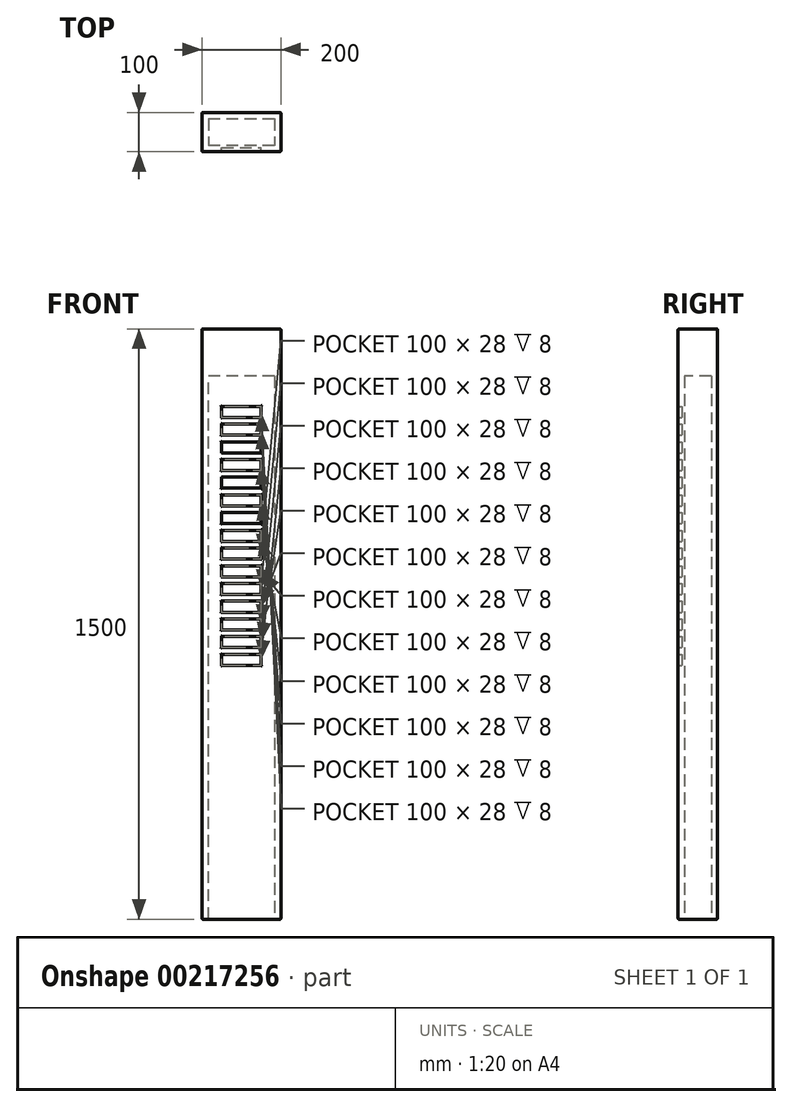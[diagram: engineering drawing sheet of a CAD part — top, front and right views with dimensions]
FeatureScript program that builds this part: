
annotation { "Feature Type Name" : "Feature", "Feature Type Description" : "" }
export const myFeature = defineFeature(function(context is Context, id is Id, definition is map)
    precondition{}
    {
        {
            var Q0;
            Q0=qCreatedBy(makeId("Front.planeOp"),FACE);
            var sketch = newSketch(context, id + "F0", { "sketchPlane" : qUnion([Q0])});
            skLineSegment(sketch, "E0.bottom", {"start": v(-100, 747.5) * mm, "end": v(100, 747.5) * mm});
            skLineSegment(sketch, "E0.top", {"start": v(-100, -752.5) * mm, "end": v(100, -752.5) * mm});
            skLineSegment(sketch, "E0.left", {"start": v(-100, 747.5) * mm, "end": v(-100, -752.5) * mm});
            skLineSegment(sketch, "E0.right", {"start": v(100, 747.5) * mm, "end": v(100, -752.5) * mm});
            skLineSegment(sketch, "E1.top", {"start": v(-50, 522.5) * mm, "end": v(50, 522.5) * mm});
            skPoint(sketch, "E1.middle", {"position": v(0, 535) * mm});
            skLineSegment(sketch, "E2.top", {"start": v(-50, 477.5) * mm, "end": v(50, 477.5) * mm});
            skPoint(sketch, "E2.middle", {"position": v(0, 490) * mm});
            skLineSegment(sketch, "E3.top", {"start": v(-50, 432.5) * mm, "end": v(50, 432.5) * mm});
            skPoint(sketch, "E3.middle", {"position": v(0, 445) * mm});
            skPoint(sketch, "E4.middle", {"position": v(0, 400) * mm});
            skLineSegment(sketch, "E5.bottom", {"start": v(-50, 387.1) * mm, "end": v(50, 387.1) * mm});
            skLineSegment(sketch, "E6.top", {"start": v(-50, 342.5) * mm, "end": v(50, 342.5) * mm});
            skPoint(sketch, "E6.middle", {"position": v(0, 355) * mm});
            skLineSegment(sketch, "E7.top", {"start": v(-50, 297.5) * mm, "end": v(50, 297.5) * mm});
            skPoint(sketch, "E7.middle", {"position": v(0, 310) * mm});
            skLineSegment(sketch, "E8.top", {"start": v(-50, 252.5) * mm, "end": v(50, 252.5) * mm});
            skPoint(sketch, "E8.middle", {"position": v(0, 265) * mm});
            skLineSegment(sketch, "E9.top", {"start": v(-50, 207.5) * mm, "end": v(50, 207.5) * mm});
            skPoint(sketch, "E9.middle", {"position": v(0, 220) * mm});
            skLineSegment(sketch, "E10.MirrorCS", {"start": v(-50, 72.5) * mm, "end": v(50, 72.5) * mm});
            skLineSegment(sketch, "E11.MirrorCS", {"start": v(-50, -107.5) * mm, "end": v(50, -107.5) * mm});
            skLineSegment(sketch, "E12.MirrorCS", {"start": v(-50, 117.5) * mm, "end": v(50, 117.5) * mm});
            skLineSegment(sketch, "E13.MirrorCS", {"start": v(-50, 27.5) * mm, "end": v(50, 27.5) * mm});
            skLineSegment(sketch, "E14.MirrorCS", {"start": v(-50, -62.5) * mm, "end": v(50, -62.5) * mm});
            skLineSegment(sketch, "E15.MirrorCS", {"start": v(-50, -17.5) * mm, "end": v(50, -17.5) * mm});
            skLineSegment(sketch, "E16.MirrorCS", {"start": v(-50, 162.5) * mm, "end": v(50, 162.5) * mm});
            skLineSegment(sketch, "E17", {"start": v(-50, 387.5) * mm, "end": v(50, 387.5) * mm});
            skLineSegment(sketch, "E18", {"start": v(50, 325.5) * mm, "end": v(-50, 325.5) * mm});
            skLineSegment(sketch, "E19", {"start": v(50, 235.5) * mm, "end": v(-50, 235.5) * mm});
            skLineSegment(sketch, "E20", {"start": v(50, 280.5) * mm, "end": v(-50, 280.5) * mm});
            skLineSegment(sketch, "E21", {"start": v(50, 190.5) * mm, "end": v(-50, 190.5) * mm});
            skLineSegment(sketch, "E22", {"start": v(50, 145.5) * mm, "end": v(-50, 145.5) * mm});
            skLineSegment(sketch, "E23", {"start": v(50, 100.5) * mm, "end": v(-50, 100.5) * mm});
            skLineSegment(sketch, "E24", {"start": v(50, 55.5) * mm, "end": v(-50, 55.5) * mm});
            skLineSegment(sketch, "E25", {"start": v(50, -34.5) * mm, "end": v(-50, -34.5) * mm});
            skLineSegment(sketch, "E26", {"start": v(50, 10.5) * mm, "end": v(-50, 10.5) * mm});
            skLineSegment(sketch, "E27", {"start": v(50, -79.5) * mm, "end": v(-50, -79.5) * mm});
            skLineSegment(sketch, "E28", {"start": v(-50, 550.5) * mm, "end": v(50, 550.5) * mm});
            skLineSegment(sketch, "E29", {"start": v(-50, 550.5) * mm, "end": v(-50, 522.5) * mm});
            skLineSegment(sketch, "E30", {"start": v(50, 550.5) * mm, "end": v(50, 522.5) * mm});
            skLineSegment(sketch, "E31", {"start": v(50, 370.5) * mm, "end": v(-50, 370.5) * mm});
            skLineSegment(sketch, "E32", {"start": v(50, 415.5) * mm, "end": v(-50, 415.5) * mm});
            skLineSegment(sketch, "E33", {"start": v(50, 460.5) * mm, "end": v(-50, 460.5) * mm});
            skLineSegment(sketch, "E34", {"start": v(50, 505.5) * mm, "end": v(-50, 505.5) * mm});
            skLineSegment(sketch, "E35", {"start": v(-50, 505.5) * mm, "end": v(-50, 477.5) * mm});
            skLineSegment(sketch, "E36", {"start": v(50, 505.5) * mm, "end": v(50, 477.5) * mm});
            skLineSegment(sketch, "E37", {"start": v(50, 460.5) * mm, "end": v(50, 432.5) * mm});
            skLineSegment(sketch, "E38", {"start": v(-50, 460.5) * mm, "end": v(-50, 432.5) * mm});
            skLineSegment(sketch, "E39", {"start": v(-50, 415.5) * mm, "end": v(-50, 387.5) * mm});
            skLineSegment(sketch, "E40", {"start": v(50, 415.5) * mm, "end": v(50, 387.5) * mm});
            skLineSegment(sketch, "E41", {"start": v(50, 370.5) * mm, "end": v(50, 342.5) * mm});
            skLineSegment(sketch, "E42", {"start": v(-50, 370.5) * mm, "end": v(-50, 342.5) * mm});
            skLineSegment(sketch, "E43", {"start": v(-50, 325.5) * mm, "end": v(-50, 297.5) * mm});
            skLineSegment(sketch, "E44", {"start": v(50, 325.5) * mm, "end": v(50, 297.5) * mm});
            skLineSegment(sketch, "E45", {"start": v(50, 280.5) * mm, "end": v(50, 252.5) * mm});
            skLineSegment(sketch, "E46", {"start": v(-50, 280.5) * mm, "end": v(-50, 252.5) * mm});
            skLineSegment(sketch, "E47", {"start": v(-50, 235.5) * mm, "end": v(-50, 207.5) * mm});
            skLineSegment(sketch, "E48", {"start": v(50, 235.5) * mm, "end": v(50, 207.5) * mm});
            skLineSegment(sketch, "E49", {"start": v(50, 190.5) * mm, "end": v(50, 162.5) * mm});
            skLineSegment(sketch, "E50", {"start": v(-50, 190.5) * mm, "end": v(-50, 162.5) * mm});
            skLineSegment(sketch, "E51", {"start": v(-50, 145.5) * mm, "end": v(-50, 117.5) * mm});
            skLineSegment(sketch, "E52", {"start": v(50, 145.5) * mm, "end": v(50, 117.5) * mm});
            skLineSegment(sketch, "E53", {"start": v(50, 100.5) * mm, "end": v(50, 72.5) * mm});
            skLineSegment(sketch, "E54", {"start": v(-50, 100.5) * mm, "end": v(-50, 72.5) * mm});
            skLineSegment(sketch, "E55", {"start": v(-50, 55.5) * mm, "end": v(-50, 27.5) * mm});
            skLineSegment(sketch, "E56", {"start": v(50, 55.5) * mm, "end": v(50, 27.5) * mm});
            skLineSegment(sketch, "E57", {"start": v(50, 10.5) * mm, "end": v(50, -17.5) * mm});
            skLineSegment(sketch, "E58", {"start": v(-50, 10.5) * mm, "end": v(-50, -17.5) * mm});
            skLineSegment(sketch, "E59", {"start": v(-50, -34.5) * mm, "end": v(-50, -62.5) * mm});
            skLineSegment(sketch, "E60", {"start": v(50, -34.5) * mm, "end": v(50, -62.5) * mm});
            skLineSegment(sketch, "E61", {"start": v(-50, -79.5) * mm, "end": v(-50, -107.5) * mm});
            skLineSegment(sketch, "E62", {"start": v(50, -79.5) * mm, "end": v(50, -107.5) * mm});
            skSolve(sketch);
        }
        {
            var Q0;
            Q0=qSketchRegion(id+"F0",true);
            var Q1;
            {var subQ0=sQuery(id+"F0.wireOp",EDGE,"E1.bottom");Q1=makeQuery(id+"F0.imprint","IMPRINT",FACE,{"disambiguationData":[TD([[makeQuery(id+"F0.imprint","IMPRINT",EDGE,{"derivedFrom":subQ0}),-1.0]])]});}
            var Q2;
            {var subQ0=sQuery(id+"F0.wireOp",EDGE,"E2.bottom");Q2=makeQuery(id+"F0.imprint","IMPRINT",FACE,{"disambiguationData":[TD([[makeQuery(id+"F0.imprint","IMPRINT",EDGE,{"derivedFrom":subQ0}),-1.0]])]});}
            var Q3;
            {var subQ0=sQuery(id+"F0.wireOp",EDGE,"E3.bottom");Q3=makeQuery(id+"F0.imprint","IMPRINT",FACE,{"disambiguationData":[TD([[makeQuery(id+"F0.imprint","IMPRINT",EDGE,{"derivedFrom":subQ0}),-1.0]])]});}
            var Q4;
            {var subQ0=sQuery(id+"F0.wireOp",EDGE,"E4.bottom");Q4=makeQuery(id+"F0.imprint","IMPRINT",FACE,{"disambiguationData":[TD([[makeQuery(id+"F0.imprint","IMPRINT",EDGE,{"derivedFrom":subQ0}),-1.0]])]});}
            var Q5;
            {var subQ0=sQuery(id+"F0.wireOp",EDGE,"pRg8M12Z-zi1p-9WqQ-BooH-lQHbHVScDsot");Q5=makeQuery(id+"F0.imprint","IMPRINT",FACE,{"disambiguationData":[TD([[makeQuery(id+"F0.imprint","IMPRINT",EDGE,{"derivedFrom":subQ0}),-1.0]])]});}
            var Q6;
            {var subQ0=sQuery(id+"F0.wireOp",EDGE,"E7.bottom");Q6=makeQuery(id+"F0.imprint","IMPRINT",FACE,{"disambiguationData":[TD([[makeQuery(id+"F0.imprint","IMPRINT",EDGE,{"derivedFrom":subQ0}),-1.0]])]});}
            var Q7;
            {var subQ0=sQuery(id+"F0.wireOp",EDGE,"E8.bottom");Q7=makeQuery(id+"F0.imprint","IMPRINT",FACE,{"disambiguationData":[TD([[makeQuery(id+"F0.imprint","IMPRINT",EDGE,{"derivedFrom":subQ0}),-1.0]])]});}
            var Q8;
            {var subQ0=sQuery(id+"F0.wireOp",EDGE,"E9.bottom");Q8=makeQuery(id+"F0.imprint","IMPRINT",FACE,{"disambiguationData":[TD([[makeQuery(id+"F0.imprint","IMPRINT",EDGE,{"derivedFrom":subQ0}),-1.0]])]});}
            var Q9;
            {var subQ0=sQuery(id+"F0.wireOp",EDGE,"edd0546f-c4f4-4053-baa7-da2036ac743645.MirrorCS");Q9=makeQuery(id+"F0.imprint","IMPRINT",FACE,{"disambiguationData":[TD([[makeQuery(id+"F0.imprint","IMPRINT",EDGE,{"derivedFrom":subQ0}),-1.0]])]});}
            var Q10;
            {var subQ0=sQuery(id+"F0.wireOp",EDGE,"edd0546f-c4f4-4053-baa7-da2036ac743633.MirrorCS");Q10=makeQuery(id+"F0.imprint","IMPRINT",FACE,{"disambiguationData":[TD([[makeQuery(id+"F0.imprint","IMPRINT",EDGE,{"derivedFrom":subQ0}),-1.0]])]});}
            var Q11;
            {var subQ0=sQuery(id+"F0.wireOp",EDGE,"edd0546f-c4f4-4053-baa7-da2036ac743644.MirrorCS");Q11=makeQuery(id+"F0.imprint","IMPRINT",FACE,{"disambiguationData":[TD([[makeQuery(id+"F0.imprint","IMPRINT",EDGE,{"derivedFrom":subQ0}),-1.0]])]});}
            var Q12;
            {var subQ0=sQuery(id+"F0.wireOp",EDGE,"edd0546f-c4f4-4053-baa7-da2036ac743629.MirrorCS");Q12=makeQuery(id+"F0.imprint","IMPRINT",FACE,{"disambiguationData":[TD([[makeQuery(id+"F0.imprint","IMPRINT",EDGE,{"derivedFrom":subQ0}),-1.0]])]});}
            var Q13;
            {var subQ0=sQuery(id+"F0.wireOp",EDGE,"edd0546f-c4f4-4053-baa7-da2036ac743631.MirrorCS");Q13=makeQuery(id+"F0.imprint","IMPRINT",FACE,{"disambiguationData":[TD([[makeQuery(id+"F0.imprint","IMPRINT",EDGE,{"derivedFrom":subQ0}),-1.0]])]});}
            var Q14;
            {var subQ0=sQuery(id+"F0.wireOp",EDGE,"edd0546f-c4f4-4053-baa7-da2036ac743634.MirrorCS");Q14=makeQuery(id+"F0.imprint","IMPRINT",FACE,{"disambiguationData":[TD([[makeQuery(id+"F0.imprint","IMPRINT",EDGE,{"derivedFrom":subQ0}),-1.0]])]});}
            var Q15;
            {var subQ0=sQuery(id+"F0.wireOp",EDGE,"edd0546f-c4f4-4053-baa7-da2036ac743620.MirrorCS");Q15=makeQuery(id+"F0.imprint","IMPRINT",FACE,{"disambiguationData":[TD([[makeQuery(id+"F0.imprint","IMPRINT",EDGE,{"derivedFrom":subQ0}),-1.0]])]});}
            var Q16;
            {var subQ0=sQuery(id+"F0.wireOp",EDGE,"edd0546f-c4f4-4053-baa7-da2036ac743627.MirrorCS");Q16=makeQuery(id+"F0.imprint","IMPRINT",FACE,{"disambiguationData":[TD([[makeQuery(id+"F0.imprint","IMPRINT",EDGE,{"derivedFrom":subQ0}),-1.0]])]});}
            var Q17;
            {var subQ0=sQuery(id+"F0.wireOp",EDGE,"lfnt6YFr-q9ma-qiqt-fEwT-RPqBtC5jHQUQ.bottom");Q17=makeQuery(id+"F0.imprint","IMPRINT",FACE,{"disambiguationData":[TD([[makeQuery(id+"F0.imprint","IMPRINT",EDGE,{"derivedFrom":subQ0}),-1.0]])]});}
            var Q18;
            {var subQ0=sQuery(id+"F0.wireOp",EDGE,"fwEZqYHB-n08x-wHNL-sWFT-xt2inMSB3fLN");Q18=makeQuery(id+"F0.imprint","IMPRINT",FACE,{"disambiguationData":[TD([[makeQuery(id+"F0.imprint","IMPRINT",EDGE,{"derivedFrom":subQ0}),1.0]])]});}
            extrude(context, id + "F1", {"entities" : qUnion([Q0, Q1, Q2, Q3, Q4, Q5, Q6, Q7, Q8, Q9, Q10, Q11, Q12, Q13, Q14, Q15, Q16, Q17, Q18]), "depth" : 10 * mm});
        }
        {
            var Q0;
            Q0=makeQuery(id+"F1.opExtrude","CAP_FACE",FACE,{"disambiguationData":[OSD([sQuery(id+"F0.wireOp",EDGE,"E0.bottom"),sQuery(id+"F0.wireOp",EDGE,"E0.top"),sQuery(id+"F0.wireOp",EDGE,"E0.left"),sQuery(id+"F0.wireOp",EDGE,"E0.right"),sQuery(id+"F0.wireOp",EDGE,"E1.top"),sQuery(id+"F0.wireOp",EDGE,"E2.top"),sQuery(id+"F0.wireOp",EDGE,"E3.top"),sQuery(id+"F0.wireOp",EDGE,"E6.top"),sQuery(id+"F0.wireOp",EDGE,"E7.top"),sQuery(id+"F0.wireOp",EDGE,"E8.top"),sQuery(id+"F0.wireOp",EDGE,"E9.top"),sQuery(id+"F0.wireOp",EDGE,"E10.MirrorCS"),sQuery(id+"F0.wireOp",EDGE,"E11.MirrorCS"),sQuery(id+"F0.wireOp",EDGE,"E12.MirrorCS"),sQuery(id+"F0.wireOp",EDGE,"E13.MirrorCS"),sQuery(id+"F0.wireOp",EDGE,"edd0546f-c4f4-4053-baa7-da2036ac743636.MirrorCS"),sQuery(id+"F0.wireOp",EDGE,"E14.MirrorCS"),sQuery(id+"F0.wireOp",EDGE,"E15.MirrorCS"),sQuery(id+"F0.wireOp",EDGE,"E16.MirrorCS"),sQuery(id+"F0.wireOp",EDGE,"lfnt6YFr-q9ma-qiqt-fEwT-RPqBtC5jHQUQ.top"),sQuery(id+"F0.wireOp",EDGE,"E17"),sQuery(id+"F0.wireOp",EDGE,"E18"),sQuery(id+"F0.wireOp",EDGE,"E19"),sQuery(id+"F0.wireOp",EDGE,"E20"),sQuery(id+"F0.wireOp",EDGE,"E21"),sQuery(id+"F0.wireOp",EDGE,"E22"),sQuery(id+"F0.wireOp",EDGE,"E23"),sQuery(id+"F0.wireOp",EDGE,"E24"),sQuery(id+"F0.wireOp",EDGE,"E25"),sQuery(id+"F0.wireOp",EDGE,"E26"),sQuery(id+"F0.wireOp",EDGE,"E27"),sQuery(id+"F0.wireOp",EDGE,"wecgm72u-QJgv-XALL-nC1d-Mx6KfSOLkq8C"),sQuery(id+"F0.wireOp",EDGE,"AfSWoiHS-NBHF-U5SL-wpfh-BBlxMHVNryGI"),sQuery(id+"F0.wireOp",EDGE,"E28"),sQuery(id+"F0.wireOp",EDGE,"E29"),sQuery(id+"F0.wireOp",EDGE,"E30"),sQuery(id+"F0.wireOp",EDGE,"E31"),sQuery(id+"F0.wireOp",EDGE,"E32"),sQuery(id+"F0.wireOp",EDGE,"E33"),sQuery(id+"F0.wireOp",EDGE,"E34"),sQuery(id+"F0.wireOp",EDGE,"KXYAlHCX-BMr1-jt93-G6wv-gBbaZAzATwQh"),sQuery(id+"F0.wireOp",EDGE,"aIZQS1V0-tCqP-P9S7-HDNZ-nWkq7dq7v80v"),sQuery(id+"F0.wireOp",EDGE,"E35"),sQuery(id+"F0.wireOp",EDGE,"E36"),sQuery(id+"F0.wireOp",EDGE,"E37"),sQuery(id+"F0.wireOp",EDGE,"E38"),sQuery(id+"F0.wireOp",EDGE,"E39"),sQuery(id+"F0.wireOp",EDGE,"E40"),sQuery(id+"F0.wireOp",EDGE,"E41"),sQuery(id+"F0.wireOp",EDGE,"E42"),sQuery(id+"F0.wireOp",EDGE,"E43"),sQuery(id+"F0.wireOp",EDGE,"E44"),sQuery(id+"F0.wireOp",EDGE,"E45"),sQuery(id+"F0.wireOp",EDGE,"E46"),sQuery(id+"F0.wireOp",EDGE,"E47"),sQuery(id+"F0.wireOp",EDGE,"E48"),sQuery(id+"F0.wireOp",EDGE,"E49"),sQuery(id+"F0.wireOp",EDGE,"E50"),sQuery(id+"F0.wireOp",EDGE,"E51"),sQuery(id+"F0.wireOp",EDGE,"E52"),sQuery(id+"F0.wireOp",EDGE,"E53"),sQuery(id+"F0.wireOp",EDGE,"E54"),sQuery(id+"F0.wireOp",EDGE,"E55"),sQuery(id+"F0.wireOp",EDGE,"E56"),sQuery(id+"F0.wireOp",EDGE,"E57"),sQuery(id+"F0.wireOp",EDGE,"E58"),sQuery(id+"F0.wireOp",EDGE,"E59"),sQuery(id+"F0.wireOp",EDGE,"E60"),sQuery(id+"F0.wireOp",EDGE,"E61"),sQuery(id+"F0.wireOp",EDGE,"E62"),sQuery(id+"F0.wireOp",EDGE,"aImYOnWc-Hrrz-Q115-OU0I-zZVykn3ZCm8c"),sQuery(id+"F0.wireOp",EDGE,"Z42Pr2mN-GHYs-NyjX-vHDr-yZRVdofESTbP")])],"isStart":true});
            var sketch = newSketch(context, id + "F2", { "sketchPlane" : qUnion([Q0])});
            skLineSegment(sketch, "E63.bottom", {"start": v(-100, 747.5) * mm, "end": v(100, 747.5) * mm});
            skLineSegment(sketch, "E63.top", {"start": v(-100, -752.5) * mm, "end": v(100, -752.5) * mm});
            skLineSegment(sketch, "E63.left", {"start": v(-100, 747.5) * mm, "end": v(-100, -752.5) * mm});
            skLineSegment(sketch, "E63.right", {"start": v(100, 747.5) * mm, "end": v(100, -752.5) * mm});
            skSolve(sketch);
        }
        {
            var Q0;
            Q0=makeQuery(id+"F2.imprint","IMPRINT",FACE,{"disambiguationData":[TD([[makeQuery(id+"F2.imprint","IMPRINT",EDGE,{"derivedFrom":sQuery(id+"F2.wireOp",EDGE,"E63.bottom")}),1.0]])]});
            var Q1;
            Q1=makeQuery(id+"F2.imprint","IMPRINT",FACE,{"disambiguationData":[TD([[makeQuery(id+"F2.imprint","IMPRINT",EDGE,{"derivedFrom":makeQuery(id+"F1.opExtrude","CAP_EDGE",EDGE,{"disambiguationData":[OSD([sQuery(id+"F0.wireOp",EDGE,"lfnt6YFr-q9ma-qiqt-fEwT-RPqBtC5jHQUQ.top")])],"isStart":true})}),-1.0]])]});
            var Q2;
            Q2=makeQuery(id+"F2.imprint","IMPRINT",FACE,{"disambiguationData":[TD([[makeQuery(id+"F2.imprint","IMPRINT",EDGE,{"derivedFrom":makeQuery(id+"F1.opExtrude","CAP_EDGE",EDGE,{"disambiguationData":[OSD([sQuery(id+"F0.wireOp",EDGE,"edd0546f-c4f4-4053-baa7-da2036ac743636.MirrorCS")])],"isStart":true})}),-1.0]])]});
            var Q3;
            Q3=makeQuery(id+"F2.imprint","IMPRINT",FACE,{"disambiguationData":[TD([[makeQuery(id+"F2.imprint","IMPRINT",EDGE,{"derivedFrom":makeQuery(id+"F1.opExtrude","CAP_EDGE",EDGE,{"disambiguationData":[OSD([sQuery(id+"F0.wireOp",EDGE,"E11.MirrorCS")])],"isStart":true})}),-1.0]])]});
            var Q4;
            Q4=makeQuery(id+"F2.imprint","IMPRINT",FACE,{"disambiguationData":[TD([[makeQuery(id+"F2.imprint","IMPRINT",EDGE,{"derivedFrom":makeQuery(id+"F1.opExtrude","CAP_EDGE",EDGE,{"disambiguationData":[OSD([sQuery(id+"F0.wireOp",EDGE,"E14.MirrorCS")])],"isStart":true})}),-1.0]])]});
            var Q5;
            Q5=makeQuery(id+"F2.imprint","IMPRINT",FACE,{"disambiguationData":[TD([[makeQuery(id+"F2.imprint","IMPRINT",EDGE,{"derivedFrom":makeQuery(id+"F1.opExtrude","CAP_EDGE",EDGE,{"disambiguationData":[OSD([sQuery(id+"F0.wireOp",EDGE,"E15.MirrorCS")])],"isStart":true})}),-1.0]])]});
            var Q6;
            Q6=makeQuery(id+"F2.imprint","IMPRINT",FACE,{"disambiguationData":[TD([[makeQuery(id+"F2.imprint","IMPRINT",EDGE,{"derivedFrom":makeQuery(id+"F1.opExtrude","CAP_EDGE",EDGE,{"disambiguationData":[OSD([sQuery(id+"F0.wireOp",EDGE,"E13.MirrorCS")])],"isStart":true})}),-1.0]])]});
            var Q7;
            Q7=makeQuery(id+"F2.imprint","IMPRINT",FACE,{"disambiguationData":[TD([[makeQuery(id+"F2.imprint","IMPRINT",EDGE,{"derivedFrom":makeQuery(id+"F1.opExtrude","CAP_EDGE",EDGE,{"disambiguationData":[OSD([sQuery(id+"F0.wireOp",EDGE,"E10.MirrorCS")])],"isStart":true})}),-1.0]])]});
            var Q8;
            Q8=makeQuery(id+"F2.imprint","IMPRINT",FACE,{"disambiguationData":[TD([[makeQuery(id+"F2.imprint","IMPRINT",EDGE,{"derivedFrom":makeQuery(id+"F1.opExtrude","CAP_EDGE",EDGE,{"disambiguationData":[OSD([sQuery(id+"F0.wireOp",EDGE,"E12.MirrorCS")])],"isStart":true})}),-1.0]])]});
            var Q9;
            Q9=makeQuery(id+"F2.imprint","IMPRINT",FACE,{"disambiguationData":[TD([[makeQuery(id+"F2.imprint","IMPRINT",EDGE,{"derivedFrom":makeQuery(id+"F1.opExtrude","CAP_EDGE",EDGE,{"disambiguationData":[OSD([sQuery(id+"F0.wireOp",EDGE,"E16.MirrorCS")])],"isStart":true})}),-1.0]])]});
            var Q10;
            Q10=makeQuery(id+"F2.imprint","IMPRINT",FACE,{"disambiguationData":[TD([[makeQuery(id+"F2.imprint","IMPRINT",EDGE,{"derivedFrom":makeQuery(id+"F1.opExtrude","CAP_EDGE",EDGE,{"disambiguationData":[OSD([sQuery(id+"F0.wireOp",EDGE,"E9.top")])],"isStart":true})}),-1.0]])]});
            var Q11;
            Q11=makeQuery(id+"F2.imprint","IMPRINT",FACE,{"disambiguationData":[TD([[makeQuery(id+"F2.imprint","IMPRINT",EDGE,{"derivedFrom":makeQuery(id+"F1.opExtrude","CAP_EDGE",EDGE,{"disambiguationData":[OSD([sQuery(id+"F0.wireOp",EDGE,"E8.top")])],"isStart":true})}),-1.0]])]});
            var Q12;
            Q12=makeQuery(id+"F2.imprint","IMPRINT",FACE,{"disambiguationData":[TD([[makeQuery(id+"F2.imprint","IMPRINT",EDGE,{"derivedFrom":makeQuery(id+"F1.opExtrude","CAP_EDGE",EDGE,{"disambiguationData":[OSD([sQuery(id+"F0.wireOp",EDGE,"E7.top")])],"isStart":true})}),-1.0]])]});
            var Q13;
            Q13=makeQuery(id+"F2.imprint","IMPRINT",FACE,{"disambiguationData":[TD([[makeQuery(id+"F2.imprint","IMPRINT",EDGE,{"derivedFrom":makeQuery(id+"F1.opExtrude","CAP_EDGE",EDGE,{"disambiguationData":[OSD([sQuery(id+"F0.wireOp",EDGE,"E6.top")])],"isStart":true})}),-1.0]])]});
            var Q14;
            Q14=makeQuery(id+"F2.imprint","IMPRINT",FACE,{"disambiguationData":[TD([[makeQuery(id+"F2.imprint","IMPRINT",EDGE,{"derivedFrom":makeQuery(id+"F1.opExtrude","CAP_EDGE",EDGE,{"disambiguationData":[OSD([sQuery(id+"F0.wireOp",EDGE,"E17")])],"isStart":true})}),-1.0]])]});
            var Q15;
            Q15=makeQuery(id+"F2.imprint","IMPRINT",FACE,{"disambiguationData":[TD([[makeQuery(id+"F2.imprint","IMPRINT",EDGE,{"derivedFrom":makeQuery(id+"F1.opExtrude","CAP_EDGE",EDGE,{"disambiguationData":[OSD([sQuery(id+"F0.wireOp",EDGE,"E3.top")])],"isStart":true})}),-1.0]])]});
            var Q16;
            Q16=makeQuery(id+"F2.imprint","IMPRINT",FACE,{"disambiguationData":[TD([[makeQuery(id+"F2.imprint","IMPRINT",EDGE,{"derivedFrom":makeQuery(id+"F1.opExtrude","CAP_EDGE",EDGE,{"disambiguationData":[OSD([sQuery(id+"F0.wireOp",EDGE,"E2.top")])],"isStart":true})}),-1.0]])]});
            var Q17;
            Q17=makeQuery(id+"F2.imprint","IMPRINT",FACE,{"disambiguationData":[TD([[makeQuery(id+"F2.imprint","IMPRINT",EDGE,{"derivedFrom":makeQuery(id+"F1.opExtrude","CAP_EDGE",EDGE,{"disambiguationData":[OSD([sQuery(id+"F0.wireOp",EDGE,"E1.top")])],"isStart":true})}),-1.0]])]});
            extrude(context, id + "F3", {"entities" : qUnion([Q0, Q1, Q2, Q3, Q4, Q5, Q6, Q7, Q8, Q9, Q10, Q11, Q12, Q13, Q14, Q15, Q16, Q17]), "operationType" : NewBodyOperationType.ADD, "depth" : 6 * mm});
        }
        {
            var Q0;
            Q0=makeQuery(id+"F3.opExtrude","CAP_FACE",FACE,{"disambiguationData":[OSD([sQuery(id+"F2.wireOp",EDGE,"E63.bottom"),sQuery(id+"F2.wireOp",EDGE,"E63.top"),sQuery(id+"F2.wireOp",EDGE,"E63.left"),sQuery(id+"F2.wireOp",EDGE,"E63.right")])],"isStart":false});
            var sketch = newSketch(context, id + "F4", { "sketchPlane" : qUnion([Q0])});
            skLineSegment(sketch, "E64", {"start": v(-100, 747.5) * mm, "end": v(100, 747.5) * mm});
            skLineSegment(sketch, "E65", {"start": v(100, 747.5) * mm, "end": v(100, 727.5) * mm});
            skLineSegment(sketch, "E66", {"start": v(-100, 627.5) * mm, "end": v(-100, -752.5) * mm});
            skLineSegment(sketch, "E67", {"start": v(100, -752.5) * mm, "end": v(100, 727.5) * mm});
            skLineSegment(sketch, "E68", {"start": v(-100, -752.5) * mm, "end": v(100, -752.5) * mm});
            skLineSegment(sketch, "E69", {"start": v(-84, -732.5) * mm, "end": v(-84, 627.5) * mm});
            skLineSegment(sketch, "E70", {"start": v(84, -732.5) * mm, "end": v(84, 627.5) * mm});
            skLineSegment(sketch, "E71", {"start": v(-84, 627.5) * mm, "end": v(84, 627.5) * mm});
            skLineSegment(sketch, "E72", {"start": v(-84, -732.5) * mm, "end": v(-84, -752.5) * mm});
            skLineSegment(sketch, "E73", {"start": v(84, -732.5) * mm, "end": v(84, -752.5) * mm});
            skSolve(sketch);
        }
        {
            var Q0;
            {var subQ0=sQuery(id+"F4.wireOp",EDGE,"o5NIRaP1-6g1h-3wY6-bDpX-dLyeNMpo0Ciy.right");Q0=makeQuery(id+"F4.imprint","IMPRINT",FACE,{"disambiguationData":[TD([[makeQuery(id+"F4.imprint","IMPRINT",EDGE,{"derivedFrom":subQ0}),-1.0]])]});}
            var Q1;
            Q1=makeQuery(id+"F4.imprint","IMPRINT",FACE,{"disambiguationData":[TD([[makeQuery(id+"F4.imprint","IMPRINT",EDGE,{"derivedFrom":sQuery(id+"F4.wireOp",EDGE,"wQEKoEdI-Ou0K-5bl5-AfoJ-Su8YN63cppm7.bottom")}),1.0]])]});
            var Q2;
            {var subQ4=sQuery(id+"F4.wireOp",EDGE,"J634U7hM-kIhP-cUew-pXYZ-ITpfumi1ZKht");Q2=makeQuery(id+"F4.imprint","IMPRINT",FACE,{"disambiguationData":[TD([[makeQuery(id+"F4.imprint","IMPRINT",EDGE,{"derivedFrom":subQ4}),1.0]])]});}
            var Q3;
            {var subQ5=sQuery(id+"F4.wireOp",EDGE,"6nLIisSD-xt2z-f9dx-YBCo-fzgKROayF0l6");Q3=makeQuery(id+"F4.imprint","IMPRINT",FACE,{"disambiguationData":[TD([[makeQuery(id+"F4.imprint","IMPRINT",EDGE,{"derivedFrom":subQ5}),-1.0]])]});}
            var Q4;
            {var subQ1=sQuery(id+"F4.wireOp",EDGE,"E64");Q4=makeQuery(id+"F4.imprint","IMPRINT",FACE,{"disambiguationData":[TD([[makeQuery(id+"F4.imprint","IMPRINT",EDGE,{"derivedFrom":subQ1}),1.0]])]});}
            extrude(context, id + "F5", {"entities" : qUnion([Q0, Q1, Q2, Q3, Q4]), "operationType" : NewBodyOperationType.ADD, "depth" : 68 * mm});
        }
        {
            var Q0;
            Q0=makeQuery(id+"F5.opExtrude","CAP_FACE",FACE,{"disambiguationData":[OSD([sQuery(id+"F2.wireOp",EDGE,"E63.left"),sQuery(id+"F4.wireOp",EDGE,"E64"),sQuery(id+"F4.wireOp",EDGE,"E65"),sQuery(id+"F4.wireOp",EDGE,"E66"),sQuery(id+"F4.wireOp",EDGE,"E67"),sQuery(id+"F4.wireOp",EDGE,"E68"),sQuery(id+"F4.wireOp",EDGE,"E69"),sQuery(id+"F4.wireOp",EDGE,"E70"),sQuery(id+"F4.wireOp",EDGE,"E71"),sQuery(id+"F4.wireOp",EDGE,"E72"),sQuery(id+"F4.wireOp",EDGE,"E73")])],"isStart":false});
            var sketch = newSketch(context, id + "F6", { "sketchPlane" : qUnion([Q0])});
            skLineSegment(sketch, "E74.bottom", {"start": v(-100, 747.5) * mm, "end": v(100, 747.5) * mm});
            skLineSegment(sketch, "E74.top", {"start": v(-100, -752.5) * mm, "end": v(100, -752.5) * mm});
            skLineSegment(sketch, "E74.left", {"start": v(-100, 747.5) * mm, "end": v(-100, -752.5) * mm});
            skLineSegment(sketch, "E74.right", {"start": v(100, 747.5) * mm, "end": v(100, -752.5) * mm});
            skSolve(sketch);
        }
        {
            var Q0;
            Q0=makeQuery(id+"F6.imprint","IMPRINT",FACE,{"disambiguationData":[TD([[makeQuery(id+"F6.imprint","IMPRINT",EDGE,{"derivedFrom":sQuery(id+"F6.wireOp",EDGE,"E74.bottom")}),1.0]])]});
            var Q1;
            Q1=makeQuery(id+"F6.imprint","IMPRINT",FACE,{"disambiguationData":[TD([[makeQuery(id+"F6.imprint","IMPRINT",EDGE,{"derivedFrom":makeQuery(id+"F5.opExtrude","CAP_EDGE",EDGE,{"disambiguationData":[OSD([sQuery(id+"F4.wireOp",EDGE,"E71")])],"isStart":false})}),-1.0]])]});
            extrude(context, id + "F7", {"entities" : qUnion([Q0, Q1]), "operationType" : NewBodyOperationType.ADD, "depth" : 16 * mm});
        }
        {
            var Q0;
            {var subQ0=sQuery(id+"F2.wireOp",EDGE,"E63.left");Q0=makeQuery(id+"F7.boolean.opBoolean","MERGE",FACE,{"derivedFrom":[makeQuery(id+"F5.boolean.opBoolean","MERGE",FACE,{"derivedFrom":[makeQuery(id+"F3.boolean.opBoolean","MERGE",FACE,{"derivedFrom":[makeQuery(id+"F1.opExtrude","SWEPT_FACE",FACE,{"disambiguationData":[OSD([sQuery(id+"F0.wireOp",EDGE,"E0.right")])]}),makeQuery(id+"F3.opExtrude","SWEPT_FACE",FACE,{"disambiguationData":[OSD([subQ0])]})]}),makeQuery(id+"F5.opExtrude","SWEPT_FACE",FACE,{"disambiguationData":[OSD([subQ0,sQuery(id+"F4.wireOp",EDGE,"E66")])]})]}),makeQuery(id+"F7.opExtrude","SWEPT_FACE",FACE,{"disambiguationData":[OSD([sQuery(id+"F6.wireOp",EDGE,"E74.left")])]})]});}
            var Q1;
            Q1=makeQuery(id+"F7.boolean.opBoolean","MERGE",FACE,{"derivedFrom":[makeQuery(id+"F5.boolean.opBoolean","MERGE",FACE,{"derivedFrom":[makeQuery(id+"F3.boolean.opBoolean","MERGE",FACE,{"derivedFrom":[makeQuery(id+"F1.opExtrude","SWEPT_FACE",FACE,{"disambiguationData":[OSD([sQuery(id+"F0.wireOp",EDGE,"E0.left")])]}),makeQuery(id+"F3.opExtrude","SWEPT_FACE",FACE,{"disambiguationData":[OSD([sQuery(id+"F2.wireOp",EDGE,"E63.right")])]})]}),makeQuery(id+"F5.opExtrude","SWEPT_FACE",FACE,{"disambiguationData":[OSD([sQuery(id+"F4.wireOp",EDGE,"E65"),sQuery(id+"F4.wireOp",EDGE,"E67")])]})]}),makeQuery(id+"F7.opExtrude","SWEPT_FACE",FACE,{"disambiguationData":[OSD([sQuery(id+"F6.wireOp",EDGE,"E74.right")])]})]});
            var Q2;
            Q2=makeQuery(id+"F1.opExtrude","CAP_FACE",FACE,{"disambiguationData":[OSD([sQuery(id+"F0.wireOp",EDGE,"E0.bottom"),sQuery(id+"F0.wireOp",EDGE,"E0.top"),sQuery(id+"F0.wireOp",EDGE,"E0.left"),sQuery(id+"F0.wireOp",EDGE,"E0.right"),sQuery(id+"F0.wireOp",EDGE,"E1.top"),sQuery(id+"F0.wireOp",EDGE,"E2.top"),sQuery(id+"F0.wireOp",EDGE,"E3.top"),sQuery(id+"F0.wireOp",EDGE,"E6.top"),sQuery(id+"F0.wireOp",EDGE,"E7.top"),sQuery(id+"F0.wireOp",EDGE,"E8.top"),sQuery(id+"F0.wireOp",EDGE,"E9.top"),sQuery(id+"F0.wireOp",EDGE,"E10.MirrorCS"),sQuery(id+"F0.wireOp",EDGE,"E11.MirrorCS"),sQuery(id+"F0.wireOp",EDGE,"E12.MirrorCS"),sQuery(id+"F0.wireOp",EDGE,"E13.MirrorCS"),sQuery(id+"F0.wireOp",EDGE,"edd0546f-c4f4-4053-baa7-da2036ac743636.MirrorCS"),sQuery(id+"F0.wireOp",EDGE,"E14.MirrorCS"),sQuery(id+"F0.wireOp",EDGE,"E15.MirrorCS"),sQuery(id+"F0.wireOp",EDGE,"E16.MirrorCS"),sQuery(id+"F0.wireOp",EDGE,"lfnt6YFr-q9ma-qiqt-fEwT-RPqBtC5jHQUQ.top"),sQuery(id+"F0.wireOp",EDGE,"E17"),sQuery(id+"F0.wireOp",EDGE,"E18"),sQuery(id+"F0.wireOp",EDGE,"E19"),sQuery(id+"F0.wireOp",EDGE,"E20"),sQuery(id+"F0.wireOp",EDGE,"E21"),sQuery(id+"F0.wireOp",EDGE,"E22"),sQuery(id+"F0.wireOp",EDGE,"E23"),sQuery(id+"F0.wireOp",EDGE,"E24"),sQuery(id+"F0.wireOp",EDGE,"E25"),sQuery(id+"F0.wireOp",EDGE,"E26"),sQuery(id+"F0.wireOp",EDGE,"E27"),sQuery(id+"F0.wireOp",EDGE,"wecgm72u-QJgv-XALL-nC1d-Mx6KfSOLkq8C"),sQuery(id+"F0.wireOp",EDGE,"AfSWoiHS-NBHF-U5SL-wpfh-BBlxMHVNryGI"),sQuery(id+"F0.wireOp",EDGE,"E28"),sQuery(id+"F0.wireOp",EDGE,"E29"),sQuery(id+"F0.wireOp",EDGE,"E30"),sQuery(id+"F0.wireOp",EDGE,"E31"),sQuery(id+"F0.wireOp",EDGE,"E32"),sQuery(id+"F0.wireOp",EDGE,"E33"),sQuery(id+"F0.wireOp",EDGE,"E34"),sQuery(id+"F0.wireOp",EDGE,"KXYAlHCX-BMr1-jt93-G6wv-gBbaZAzATwQh"),sQuery(id+"F0.wireOp",EDGE,"aIZQS1V0-tCqP-P9S7-HDNZ-nWkq7dq7v80v"),sQuery(id+"F0.wireOp",EDGE,"E35"),sQuery(id+"F0.wireOp",EDGE,"E36"),sQuery(id+"F0.wireOp",EDGE,"E37"),sQuery(id+"F0.wireOp",EDGE,"E38"),sQuery(id+"F0.wireOp",EDGE,"E39"),sQuery(id+"F0.wireOp",EDGE,"E40"),sQuery(id+"F0.wireOp",EDGE,"E41"),sQuery(id+"F0.wireOp",EDGE,"E42"),sQuery(id+"F0.wireOp",EDGE,"E43"),sQuery(id+"F0.wireOp",EDGE,"E44"),sQuery(id+"F0.wireOp",EDGE,"E45"),sQuery(id+"F0.wireOp",EDGE,"E46"),sQuery(id+"F0.wireOp",EDGE,"E47"),sQuery(id+"F0.wireOp",EDGE,"E48"),sQuery(id+"F0.wireOp",EDGE,"E49"),sQuery(id+"F0.wireOp",EDGE,"E50"),sQuery(id+"F0.wireOp",EDGE,"E51"),sQuery(id+"F0.wireOp",EDGE,"E52"),sQuery(id+"F0.wireOp",EDGE,"E53"),sQuery(id+"F0.wireOp",EDGE,"E54"),sQuery(id+"F0.wireOp",EDGE,"E55"),sQuery(id+"F0.wireOp",EDGE,"E56"),sQuery(id+"F0.wireOp",EDGE,"E57"),sQuery(id+"F0.wireOp",EDGE,"E58"),sQuery(id+"F0.wireOp",EDGE,"E59"),sQuery(id+"F0.wireOp",EDGE,"E60"),sQuery(id+"F0.wireOp",EDGE,"E61"),sQuery(id+"F0.wireOp",EDGE,"E62"),sQuery(id+"F0.wireOp",EDGE,"aImYOnWc-Hrrz-Q115-OU0I-zZVykn3ZCm8c"),sQuery(id+"F0.wireOp",EDGE,"Z42Pr2mN-GHYs-NyjX-vHDr-yZRVdofESTbP")])],"isStart":false});
            var Q3;
            Q3=makeQuery(id+"F7.opExtrude","CAP_FACE",FACE,{"disambiguationData":[OSD([sQuery(id+"F6.wireOp",EDGE,"E74.bottom"),sQuery(id+"F6.wireOp",EDGE,"E74.top"),sQuery(id+"F6.wireOp",EDGE,"E74.left"),sQuery(id+"F6.wireOp",EDGE,"E74.right")])],"isStart":false});
            fillet(context, id + "F8", {"entities" : qUnion([Q0, Q1, Q2, Q3]), "radius" : 2 * mm, "tangentPropagation" : true, "allowEdgeOverflow" : false});
        }
    });
